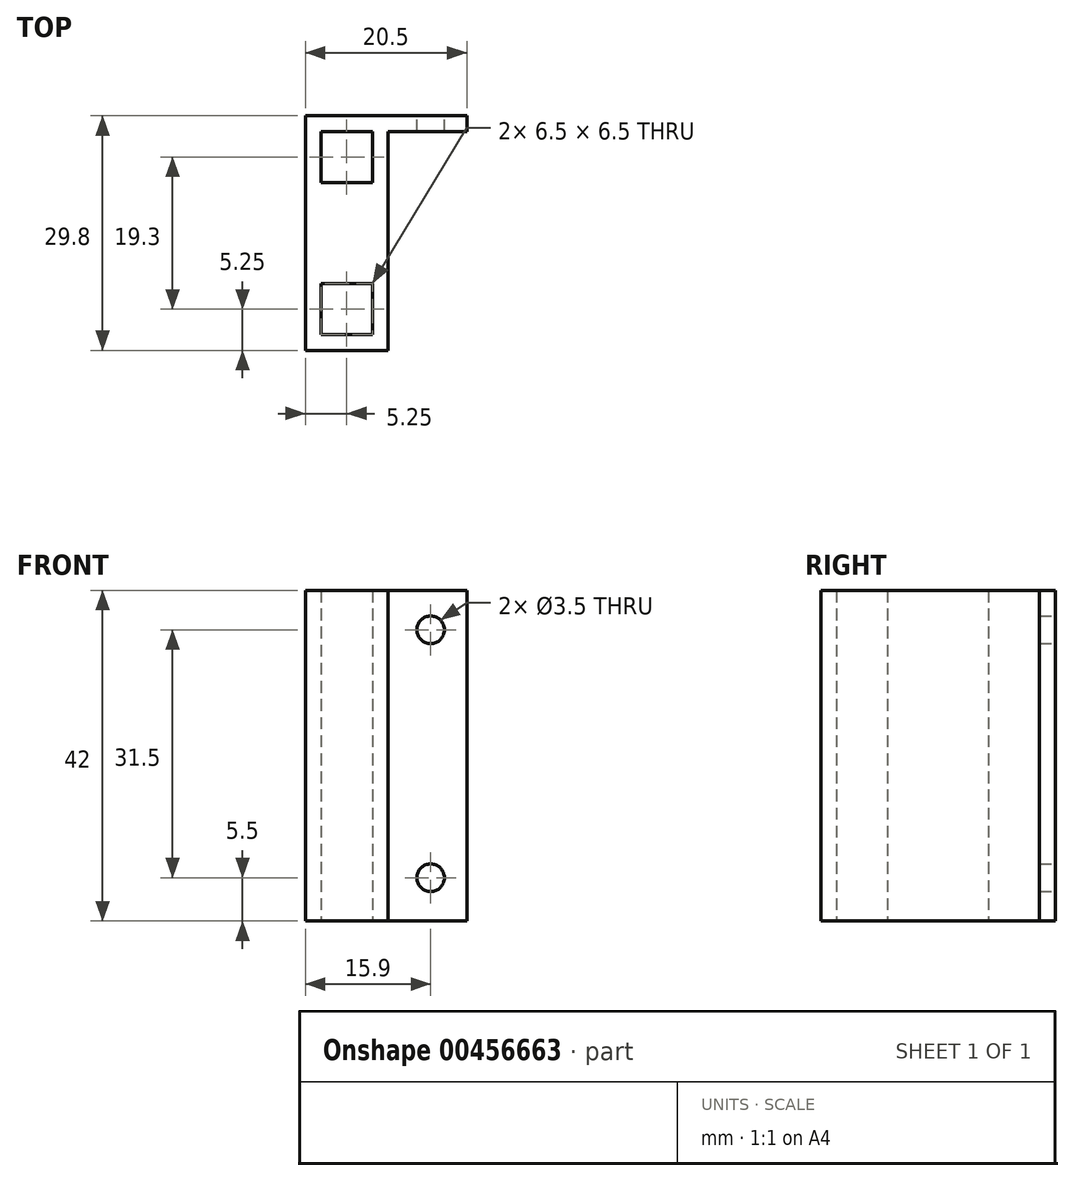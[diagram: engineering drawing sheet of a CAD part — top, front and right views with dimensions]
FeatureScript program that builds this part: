
annotation { "Feature Type Name" : "Feature", "Feature Type Description" : "" }
export const myFeature = defineFeature(function(context is Context, id is Id, definition is map)
    precondition{}
    {
        {
            var Q0;
            Q0=qCreatedBy(makeId("Top.planeOp"),FACE);
            var sketch = newSketch(context, id + "F0", { "sketchPlane" : qUnion([Q0])});
            skLineSegment(sketch, "E0.bottom", {"start": v(0, 0) * mm, "end": v(20.5, 0) * mm});
            skLineSegment(sketch, "E0.top", {"start": v(0, -29.8) * mm, "end": v(20.5, -29.8) * mm});
            skLineSegment(sketch, "E0.left", {"start": v(0, 0) * mm, "end": v(0, -29.8) * mm});
            skLineSegment(sketch, "E0.right", {"start": v(20.5, 0) * mm, "end": v(20.5, -29.8) * mm});
            skLineSegment(sketch, "E1.bottom", {"start": v(2, -2) * mm, "end": v(8.5, -2) * mm});
            skLineSegment(sketch, "E1.top", {"start": v(2, -8.5) * mm, "end": v(8.5, -8.5) * mm});
            skLineSegment(sketch, "E1.left", {"start": v(2, -2) * mm, "end": v(2, -8.5) * mm});
            skLineSegment(sketch, "E1.right", {"start": v(8.5, -2) * mm, "end": v(8.5, -8.5) * mm});
            skLineSegment(sketch, "E2.bottom", {"start": v(2, -21.3) * mm, "end": v(8.5, -21.3) * mm});
            skLineSegment(sketch, "E2.top", {"start": v(2, -27.8) * mm, "end": v(8.5, -27.8) * mm});
            skLineSegment(sketch, "E2.left", {"start": v(2, -21.3) * mm, "end": v(2, -27.8) * mm});
            skLineSegment(sketch, "E2.right", {"start": v(8.5, -21.3) * mm, "end": v(8.5, -27.8) * mm});
            skLineSegment(sketch, "E3.bottom", {"start": v(20.5, -2) * mm, "end": v(10.5, -2) * mm});
            skLineSegment(sketch, "E3.top", {"start": v(20.5, -29.8) * mm, "end": v(10.5, -29.8) * mm});
            skLineSegment(sketch, "E3.left", {"start": v(20.5, -2) * mm, "end": v(20.5, -29.8) * mm});
            skLineSegment(sketch, "E3.right", {"start": v(10.5, -2) * mm, "end": v(10.5, -29.8) * mm});
            skSolve(sketch);
        }
        {
            var Q0;
            Q0=makeQuery(id+"F0.imprint","IMPRINT",FACE,{"disambiguationData":[TD([[makeQuery(id+"F0.imprint","IMPRINT",EDGE,{"derivedFrom":sQuery(id+"F0.wireOp",EDGE,"E0.bottom")}),-1.0]])]});
            extrude(context, id + "F1", {"entities" : qUnion([Q0]), "depth" : 42 * mm});
        }
        {
            var Q0;
            Q0=makeQuery(id+"F1.opExtrude","SWEPT_FACE",FACE,{"disambiguationData":[OSD([sQuery(id+"F0.wireOp",EDGE,"E0.bottom")])]});
            var sketch = newSketch(context, id + "F2", { "sketchPlane" : qUnion([Q0])});
            skLineSegment(sketch, "E4.bottom", {"start": v(0, 0) * mm, "end": v(-15.9, 0) * mm});
            skLineSegment(sketch, "E4.top", {"start": v(0, 5.5) * mm, "end": v(-15.9, 5.5) * mm});
            skLineSegment(sketch, "E4.left", {"start": v(0, 0) * mm, "end": v(0, 5.5) * mm});
            skLineSegment(sketch, "E4.right", {"start": v(-15.9, 0) * mm, "end": v(-15.9, 5.5) * mm});
            skCircle(sketch, "E5", {"center": v(-15.9, 5.5) * mm, "radius": 1.75 * mm});
            skLineSegment(sketch, "E6.top", {"start": v(0, 37) * mm, "end": v(-15.9, 37) * mm});
            skLineSegment(sketch, "E6.left", {"start": v(0, 0) * mm, "end": v(0, 37) * mm});
            skLineSegment(sketch, "E6.right", {"start": v(-15.9, 0) * mm, "end": v(-15.9, 37) * mm});
            skCircle(sketch, "E7", {"center": v(-15.9, 37) * mm, "radius": 1.75 * mm});
            skSolve(sketch);
        }
        {
            var Q0;
            {var subQ0=sQuery(id+"F2.wireOp",EDGE,"E6.right");var subQ1=sQuery(id+"F2.wireOp",EDGE,"E4.top");var subQ2=makeQuery(id+"F2.imprint","INTERSECT",VERTEX,{"derivedFrom":[subQ1,subQ0]});Q0=makeQuery(id+"F2.imprint","IMPRINT",FACE,{"disambiguationData":[TD([[makeQuery(id+"F2.imprint","IMPRINT",EDGE,{"disambiguationData":[TD([[subQ2,1.0]])],"derivedFrom":subQ1}),-1.0]])]});}
            var Q1;
            {var subQ0=sQuery(id+"F2.wireOp",EDGE,"E6.right");var subQ1=sQuery(id+"F2.wireOp",EDGE,"E4.top");var subQ2=makeQuery(id+"F2.imprint","INTERSECT",VERTEX,{"derivedFrom":[subQ1,subQ0]});Q1=makeQuery(id+"F2.imprint","IMPRINT",FACE,{"disambiguationData":[TD([[makeQuery(id+"F2.imprint","IMPRINT",EDGE,{"disambiguationData":[TD([[subQ2,1.0]])],"derivedFrom":subQ1}),1.0]])]});}
            var Q2;
            {var subQ0=sQuery(id+"F2.wireOp",EDGE,"E6.right");var subQ1=sQuery(id+"F2.wireOp",EDGE,"E5");var subQ2=makeQuery(id+"F2.imprint","INTERSECT",VERTEX,{"disambiguationData":[OD(0.0)],"derivedFrom":[subQ1,subQ0]});Q2=makeQuery(id+"F2.imprint","IMPRINT",FACE,{"disambiguationData":[TD([[makeQuery(id+"F2.imprint","IMPRINT",EDGE,{"disambiguationData":[TD([[subQ2,-1.0]])],"derivedFrom":subQ1}),1.0]])]});}
            var Q3;
            {var subQ0=sQuery(id+"F2.wireOp",EDGE,"E6.right");var subQ1=sQuery(id+"F2.wireOp",EDGE,"E6.top");var subQ2=makeQuery(id+"F2.imprint","INTERSECT",VERTEX,{"derivedFrom":[subQ1,subQ0]});Q3=makeQuery(id+"F2.imprint","IMPRINT",FACE,{"disambiguationData":[TD([[makeQuery(id+"F2.imprint","IMPRINT",EDGE,{"disambiguationData":[TD([[subQ2,1.0]])],"derivedFrom":subQ1}),1.0]])]});}
            var Q4;
            {var subQ0=sQuery(id+"F2.wireOp",EDGE,"E6.right");var subQ1=sQuery(id+"F2.wireOp",EDGE,"E6.top");var subQ2=makeQuery(id+"F2.imprint","INTERSECT",VERTEX,{"derivedFrom":[subQ1,subQ0]});Q4=makeQuery(id+"F2.imprint","IMPRINT",FACE,{"disambiguationData":[TD([[makeQuery(id+"F2.imprint","IMPRINT",EDGE,{"disambiguationData":[TD([[subQ2,1.0]])],"derivedFrom":subQ1}),-1.0]])]});}
            extrude(context, id + "F3", {"entities" : qUnion([Q0, Q1, Q2, Q3, Q4]), "operationType" : NewBodyOperationType.REMOVE, "endBound" : BoundingType.THROUGH_ALL, "oppositeDirection" : true, "depth" : 25 * mm});
        }
    });
